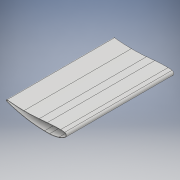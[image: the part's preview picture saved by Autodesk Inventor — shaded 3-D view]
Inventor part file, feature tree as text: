
AUTODESK INVENTOR PART (.ipt)
format: ipt  version: 2018.2 (Build 222227000, 227)  size: 143,872 bytes
history: native  units: mm
features: extrude x1, shell x1, sketch x1, projected_geometry x1
ambient origin geometry x8: Origin, YZ Plane, XZ Plane, XY Plane, X Axis, Y Axis, Z Axis, Center Point
bodies: Body1 (feature_tree)
feature tree (4):
  extrude  "押し出し1"  Depth=225.0mm TaperAngle=0.0deg
  shell  "シェル1"  Thickness=1.0mm
  sketch  "スケッチ1"
  projected_geometry  "投影ループ1"
